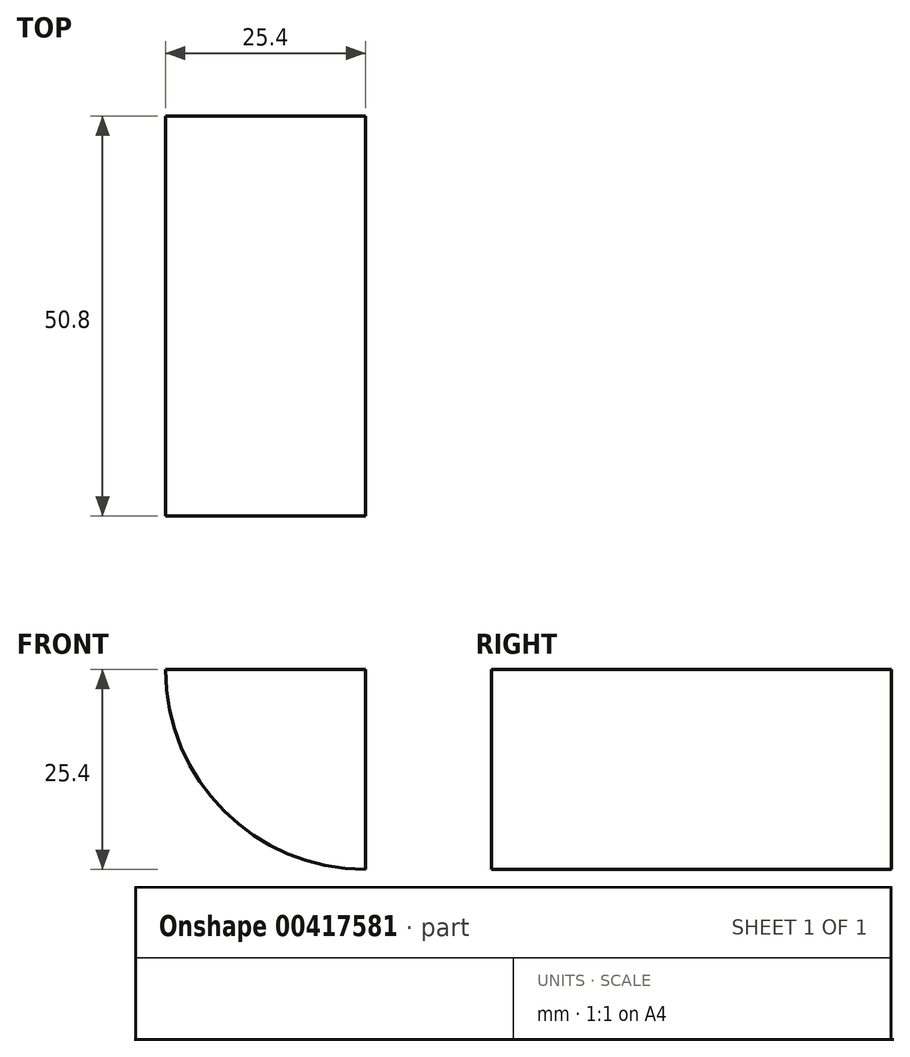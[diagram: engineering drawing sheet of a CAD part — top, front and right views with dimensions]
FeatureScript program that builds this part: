
annotation { "Feature Type Name" : "Feature", "Feature Type Description" : "" }
export const myFeature = defineFeature(function(context is Context, id is Id, definition is map)
    precondition{}
    {
        {
            var Q0;
            Q0=qCreatedBy(makeId("Front.planeOp"),FACE);
            var sketch = newSketch(context, id + "F0", { "sketchPlane" : qUnion([Q0])});
            skLineSegment(sketch, "E0.bottom", {"start": v(0, 0) * mm, "end": v(-25.4, 0) * mm});
            skLineSegment(sketch, "E0.top", {"start": v(0, 0) * mm, "end": v(-25.4, 0) * mm});
            skLineSegment(sketch, "E0.left", {"start": v(0, 0) * mm, "end": v(0, 0) * mm});
            skLineSegment(sketch, "E0.right", {"start": v(-25.4, 0) * mm, "end": v(-25.4, 0) * mm});
            skLineSegment(sketch, "E1.bottom", {"start": v(-25.4, 0) * mm, "end": v(25.4, 0) * mm});
            skLineSegment(sketch, "E1.top", {"start": v(-25.4, 50.8) * mm, "end": v(25.4, 50.8) * mm});
            skLineSegment(sketch, "E1.left", {"start": v(-25.4, 0) * mm, "end": v(-25.4, 50.8) * mm});
            skLineSegment(sketch, "E1.right", {"start": v(25.4, 0) * mm, "end": v(25.4, 50.8) * mm});
            skSolve(sketch);
        }
        {
            var Q0;
            Q0=makeQuery(id+"F0.imprint","IMPRINT",FACE,{"disambiguationData":[TD([[makeQuery(id+"F0.imprint","IMPRINT",EDGE,{"derivedFrom":sQuery(id+"F0.wireOp",EDGE,"E1.top")}),-1.0]])]});
            extrude(context, id + "F1", {"entities" : qUnion([Q0]), "depth" : 50.8 * mm});
        }
        {
            var Q0;
            Q0=makeQuery(id+"F1.opExtrude","CAP_FACE",FACE,{"disambiguationData":[OSD([sQuery(id+"F0.wireOp",EDGE,"E1.bottom"),sQuery(id+"F0.wireOp",EDGE,"E1.top"),sQuery(id+"F0.wireOp",EDGE,"E1.left"),sQuery(id+"F0.wireOp",EDGE,"E1.right")])],"isStart":false});
            var sketch = newSketch(context, id + "F2", { "sketchPlane" : qUnion([Q0])});
            skArc(sketch, "E2", {"start": v(25.4, 25.4) * mm, "mid": v(7.44, 32.84) * mm, "end": v(0, 50.8) * mm});
            skSolve(sketch);
        }
        {
            var Q0;
            {var subQ0=sQuery(id+"F2.wireOp",EDGE,"E2");Q0=makeQuery(id+"F2.imprint","IMPRINT",FACE,{"disambiguationData":[TD([[makeQuery(id+"F2.imprint","IMPRINT",EDGE,{"derivedFrom":subQ0}),-1.0]])]});}
            extrude(context, id + "F3", {"entities" : qUnion([Q0]), "operationType" : NewBodyOperationType.REMOVE, "oppositeDirection" : true, "depth" : 50.8 * mm});
        }
    });
